# Revit family: Rohrschelle Maxima PSM, halb Zoll, Ø120-275, Gummi
name_source: partatom
category: HLS-Bauteile
revit_build: Autodesk Revit 2017 (Build: 20190507_1515(x64)
units: mm (PartAtom-declared; Revit-internal decimal feet)

## family parameters
Arbeitsebenenbasiert = Nein
Beim Laden mit Abzugskörper schneiden = Nein
Bemaßung runder Anschluss = Durchmesser verwenden
Gemeinsam genutzt = Ja
Immer vertikal = Nein
Raumberechnungspunkt = Nein
Teiletyp = Normal

## types (15) — shared parameters
A = 25 mm  [stored 0.082021 ft]
Anschluss = 1/2''
Anschlußhöhe = 25 mm
Bauart = zweiteilig
Baustoffklasse = B2
Brandschutz = RAL-GZ 656
DF1 = 30 mm  [stored 0.0984252 ft]
DF2 = 34 mm
DS = 6 mm  [stored 0.019685 ft]
DVS = 18 mm  [stored 0.0590551 ft]
Dämmstärke = 6 mm  [stored 0.019685 ft]
Fabrikat = MEFA
Farbe Schalldämmeinlage = schwarz
Firma = MEFA Befestigungs- und Montagesysteme GmbH
HGA = 15 mm  [stored 0.0492126 ft]
Kurztext1 = Rohrschelle Maxima PSM 35x4,0
MB = 35 mm  [stored 0.114829 ft]
MD = 4 mm  [stored 0.0131234 ft]
Material = Stahl
Material Schalldämmeinlage = TPE
Materialmaße = 35x4,0 mm
Materialname = S235
Mengeneinheit = St
Oberflaeche = galvanisch verzinkt
Schalldämmeinlage = Gummi
Verschluss = Pendelsteckmuttern
Verschluss-Schraube = M10
max. Temperaturbeständigkeit = 100 °C
max. zul. Last = 5.00 kN
max. zul. Last horizontal = 0.00 kN
max. zul. Last vertikal = 0.00 kN
vpe = 1 St
zero-valued in all types: Nennweite DN Rohr, Rohraußendurchmesser, Stärke Material

## per-type parameters (varying)
| type | AB | Achsabstand | Artikelnummer | B | Breite | D | D0 | Dmax | Dmin | EAN | Gewicht | Gewicht pro Bauteil | H | Kurztext2 | R | RM | Rohraußendurchmesser Zoll | S | max. Höhe | max. Rohraußendurchmesser | min. Rohraußendurchmesser |
| Maxima PSM, 1/2", Ø120-125, Gummi | 5 mm  [stored 0.0164042 ft] | 179 mm | 0082146 | 209 mm | 209 mm | 125 mm  [stored 0.410105 ft] | 137 mm | 125 mm  [stored 0.410105 ft] | 120 mm  [stored 0.393701 ft] | 4250928406408 | 0.80 kg | 0.80 kg | 160 mm | 120 - 125 mm 1/2'' TPE | 69 mm | 73 mm | Zoll | 179 mm | 160 mm | 125 mm  [stored 0.410105 ft] | 120 mm  [stored 0.393701 ft] |
| Maxima PSM, 1/2", Ø127-132, Gummi | 5 mm  [stored 0.0164042 ft] | 186 mm | 0082155 | 216 mm | 216 mm | 132 mm  [stored 0.433071 ft] | 144 mm | 132 mm  [stored 0.433071 ft] | 127 mm | 4250928406446 | 0.84 kg | 0.84 kg | 167 mm | 127 - 132 mm 1/2'' TPE | 72 mm  [stored 0.23622 ft] | 76 mm  [stored 0.249344 ft] | Zoll | 186 mm | 167 mm | 132 mm  [stored 0.433071 ft] | 127 mm |
| Maxima PSM, 1/2", Ø133-136, Gummi | 3 mm  [stored 0.00984252 ft] | 190 mm | 0082163 | 220 mm | 220 mm | 136 mm | 148 mm | 136 mm | 133 mm  [stored 0.436352 ft] | 4250928406460 | 0.86 kg | 0.86 kg | 171 mm | 133 - 136 mm 1/2'' TPE | 74 mm  [stored 0.242782 ft] | 78 mm  [stored 0.255906 ft] | Zoll | 190 mm | 171 mm | 136 mm | 133 mm  [stored 0.436352 ft] |
| Maxima PSM, 1/2", Ø137-142, Gummi | 5 mm  [stored 0.0164042 ft] | 196 mm | 0082168 | 226 mm | 226 mm | 142 mm | 154 mm | 142 mm | 137 mm | 4250928406477 | 0.88 kg | 0.88 kg | 177 mm | 137 - 142 mm 1/2'' TPE | 77 mm  [stored 0.252625 ft] | 81 mm | 5 Zoll | 196 mm | 177 mm | 142 mm | 137 mm |
| Maxima PSM, 1/2", Ø145-150, Gummi | 5 mm  [stored 0.0164042 ft] | 204 mm | 0082170 | 234 mm | 234 mm | 150 mm | 162 mm | 150 mm | 145 mm | 4250928406484 | 0.92 kg | 0.92 kg | 185 mm | 145 - 150 mm 1/2'' TPE | 81 mm | 85 mm | Zoll | 204 mm | 185 mm | 150 mm | 145 mm |
| Maxima PSM, 1/2", Ø152-156, Gummi | 4 mm  [stored 0.0131234 ft] | 210 mm | 0082197 | 240 mm | 240 mm | 156 mm | 168 mm | 156 mm | 152 mm | 4250928406521 | 0.95 kg | 0.95 kg | 191 mm | 152 - 156 mm 1/2'' TPE | 84 mm  [stored 0.275591 ft] | 88 mm | Zoll | 210 mm | 191 mm | 156 mm | 152 mm |
| Maxima PSM, 1/2", Ø158-163, Gummi | 5 mm  [stored 0.0164042 ft] | 217 mm | 0082201 | 247 mm | 247 mm | 163 mm | 175 mm | 163 mm | 158 mm | 4250928406538 | 0.97 kg | 0.97 kg | 198 mm | 158 - 163 mm 1/2'' TPE | 88 mm | 92 mm | Zoll | 217 mm | 198 mm | 163 mm | 158 mm |
| Maxima PSM, 1/2", Ø164-168, Gummi | 4 mm  [stored 0.0131234 ft] | 222 mm | 0082210 | 252 mm | 252 mm | 168 mm | 180 mm | 168 mm | 164 mm | 4250928406545 | 1.00 kg | 1.00 kg | 203 mm | 164 - 168 mm 1/2'' TPE | 90 mm | 94 mm | 6 Zoll | 222 mm | 203 mm | 168 mm | 164 mm |
| Maxima PSM, 1/2", Ø190-194, Gummi | 4 mm  [stored 0.0131234 ft] | 248 mm | 0082250 | 278 mm | 278 mm | 194 mm | 206 mm | 194 mm | 190 mm | 4250928406576 | 1.12 kg | 1.12 kg | 229 mm | 190 - 194 mm 1/2'' TPE | 103 mm  [stored 0.337927 ft] | 107 mm  [stored 0.35105 ft] | Zoll | 248 mm | 229 mm | 194 mm | 190 mm |
| Maxima PSM, 1/2", Ø198-203, Gummi | 5 mm  [stored 0.0164042 ft] | 257 mm | 0082254 | 287 mm | 287 mm | 203 mm | 215 mm | 203 mm | 198 mm | 4250928406583 | 1.15 kg | 1.15 kg | 238 mm | 198 - 203 mm 1/2'' TPE | 108 mm | 112 mm | Zoll | 257 mm | 238 mm | 203 mm | 198 mm |
| Maxima PSM, 1/2", Ø207-213, Gummi | 6 mm  [stored 0.019685 ft] | 267 mm | 0082290 | 297 mm | 297 mm | 213 mm | 225 mm | 213 mm | 207 mm | 4250928406606 | 1.19 kg | 1.19 kg | 248 mm | 207 - 213 mm 1/2'' TPE | 113 mm | 117 mm | Zoll | 267 mm | 248 mm | 213 mm | 207 mm |
| Maxima PSM, 1/2", Ø219-223, Gummi | 4 mm  [stored 0.0131234 ft] | 277 mm | 0082297 | 307 mm | 307 mm | 223 mm | 235 mm | 223 mm | 219 mm | 4250928406620 | 1.24 kg | 1.24 kg | 258 mm | 219 - 223 mm 1/2'' TPE | 118 mm | 122 mm | 8 Zoll | 277 mm | 258 mm | 223 mm | 219 mm |
| Maxima PSM, 1/2", Ø225-230, Gummi | 5 mm  [stored 0.0164042 ft] | 284 mm | 0082309 | 314 mm | 314 mm | 230 mm | 242 mm | 230 mm | 225 mm | 4250928406637 | 1.27 kg | 1.27 kg | 265 mm | 225 - 230 mm 1/2'' TPE | 121 mm  [stored 0.396982 ft] | 125 mm  [stored 0.410105 ft] | Zoll | 284 mm | 265 mm | 230 mm | 225 mm |
| Maxima PSM, 1/2", Ø242-246, Gummi | 4 mm  [stored 0.0131234 ft] | 300 mm | 0082327 | 330 mm | 330 mm | 246 mm | 258 mm | 246 mm | 242 mm | 4250928406651 | 1.35 kg | 1.35 kg | 281 mm | 242 - 246 mm 1/2'' TPE | 129 mm | 133 mm  [stored 0.436352 ft] | Zoll | 300 mm | 281 mm | 246 mm | 242 mm |
| Maxima PSM, 1/2", Ø270-275, Gummi | 5 mm  [stored 0.0164042 ft] | 329 mm | 0082370 | 359 mm | 359 mm | 275 mm | 287 mm | 275 mm | 270 mm | 4250928406675 | 1.47 kg | 1.47 kg | 310 mm | 270 - 275 mm 1/2'' TPE | 144 mm | 148 mm | 10 Zoll | 329 mm | 310 mm | 275 mm | 270 mm |

note: [stored X ft] marks values corroborated as IEEE doubles in the binary element streams (Revit-internal decimal feet)
